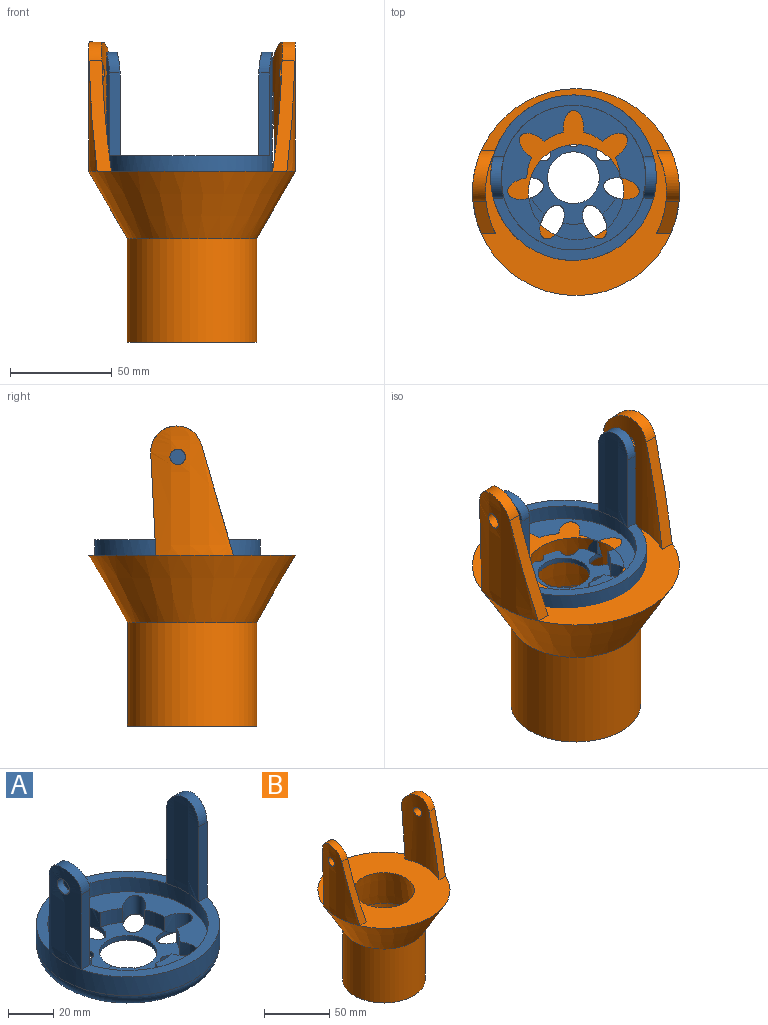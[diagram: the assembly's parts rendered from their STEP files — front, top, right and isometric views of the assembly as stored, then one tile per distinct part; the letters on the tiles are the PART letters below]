
ASSEMBLY  parts=2 mates=1
PART A: 37 faces, bbox 88x88x68.6 mm
  f0: extruded ~50.8x20.32mm, area 952.4mm2, adj f2,f3,f6,f23,f35
  f1: plane 40.64x5.27mm, normal (0,1,0), area 214.2mm2, adj f4,f24,f30,f32
  f2: plane 40.64x5.27mm, normal (0,1,0), area 214.2mm2, adj f0,f3,f24,f31
  f3: cylinder r=10.16mm len=20.32mm, axis (-1,0,0), area 165.2mm2, adj f0,f2,f6,f31
  f4: cylinder r=10.16mm len=20.32mm, axis (-1,0,0), area 165.2mm2, adj f1,f5,f30,f32
  f5: plane 40.64x5.27mm, normal (0,-1,0), area 214.2mm2, adj f4,f7,f30,f32
  f6: plane 40.64x5.27mm, normal (0,-1,0), area 214.2mm2, adj f0,f3,f7,f31
  f7: plane 78.7x30.48mm, normal (0,0,1), area 503.6mm2, adj f5,f6,f23,f25
  f8: cylinder r=22.86mm len=10.14mm, axis (0,0,1), area 80mm2, adj f9,f11,f26,f28
  f9: extruded ~15.27x13.63mm, area 311.7mm2, adj f8,f21,f26,f27,f28
  f10: cylinder r=22.86mm len=8.13mm, axis (0,0,1), area 80mm2, adj f11,f13,f26,f28
  f11: extruded ~17.44x10.67mm, area 311.7mm2, adj f8,f10,f21,f26,f28
  f12: cylinder r=22.86mm len=10.4mm, axis (0,0,1), area 80mm2, adj f13,f15,f26,f28
  f13: extruded ~16.57x11.93mm, area 311.7mm2, adj f10,f12,f21,f26,f28
  f14: cylinder r=22.86mm len=8.13mm, axis (0,0,1), area 80mm2, adj f15,f17,f26,f28
  f15: extruded ~16.57x11.93mm, area 311.7mm2, adj f12,f14,f21,f26,f28
  f16: cylinder r=22.86mm len=10.14mm, axis (0,0,1), area 80mm2, adj f17,f19,f26,f28
  f17: extruded ~17.44x10.67mm, area 311.7mm2, adj f14,f16,f21,f26,f28
  f18: cylinder r=22.86mm len=9.37mm, axis (0,0,1), area 80mm2, adj f19,f26,f28,f29
  f19: extruded ~15.27x13.63mm, area 311.7mm2, adj f16,f18,f21,f26,f28
  f20: cylinder r=12.7mm len=25.4mm, axis (0,0,1), area 202.7mm2, adj f21,f28
  f21: plane 66.04x66.04mm, normal (0,0,-1), area 1925.5mm2, adj f9,f11,f13,f15,f17,f19,f20,f22
  f22: torus R=33.02mm, axis (0,0,1), area 2848.1mm2, adj f21,f23
  f23: cylinder r=40.64mm len=81.28mm, axis (0,0,1), area 2594.3mm2, adj f0,f7,f22,f24,f30
  f24: plane 78.7x30.48mm, normal (0,0,1), area 503.6mm2, adj f1,f2,f23,f25
  f25: cylinder r=35.56mm len=71.12mm, axis (0,0,1), area 1702.5mm2, adj f7,f24,f26,f31,f32
  f26: plane 71.12x71.12mm, normal (0,0,1), area 1731.4mm2, adj f8,f9,f10,f11,f12,f13,f14,f15
  f27: cylinder r=22.86mm len=9.37mm, axis (0,0,1), area 80mm2, adj f9,f26,f28,f29
  f28: plane 45.72x45.17mm, normal (0,0,1), area 741.3mm2, adj f8,f9,f10,f11,f12,f13,f14,f15
  f29: extruded ~17.78x10.16mm, area 311.7mm2, adj f18,f21,f26,f27,f28
  f30: extruded ~50.8x20.32mm, area 952.5mm2, adj f1,f4,f5,f23,f33
  f31: extruded ~50.8x20.32mm, area 1001.3mm2, adj f2,f3,f6,f25
  f32: extruded ~50.8x20.32mm, area 1001.4mm2, adj f1,f4,f5,f25
  f33: cylinder r=3.81mm len=7.62mm, axis (1,0,0), area 89.1mm2, adj f30,f34
  f34: plane 7.62x7.62mm, normal (1,0,0), area 45.6mm2, adj f33
  f35: cylinder r=3.81mm len=7.62mm, axis (-1,0,0), area 89.1mm2, adj f0,f36
  f36: plane 7.62x7.62mm, normal (-1,0,0), area 45.6mm2, adj f35
PART B: 18 faces, bbox 102x102x147.7 mm
  f0: plane 50.54x8.42mm, normal (0,1,-0.05), area 348.2mm2, adj f3,f8,f12,f14
  f1: plane 50.54x8.42mm, normal (0,1,-0.05), area 348.2mm2, adj f2,f8,f13,f15
  f2: cylinder r=12.7mm len=24.9mm, axis (-1,0,0), area 243.6mm2, adj f1,f4,f13,f15
  f3: cylinder r=12.7mm len=24.9mm, axis (-1,0,0), area 243.6mm2, adj f0,f5,f12,f14
  f4: plane 54.66x16.07mm, normal (0,-0.96,0.28), area 374.5mm2, adj f2,f8,f13,f15
  f5: plane 54.66x16.07mm, normal (0,-0.96,0.28), area 374.5mm2, adj f3,f8,f12,f14
  f6: cylinder r=31.75mm len=63.5mm, axis (0,0,1), area 10134.1mm2, adj f7,f11
  f7: cone r=50.8mm half-angle=30deg, axis (0,0,1), area 9880.8mm2, adj f6,f8,f12,f13
  f8: plane 101.6x95.17mm, normal (0,0,1), area 5890.2mm2, adj f0,f1,f4,f5,f7,f9,f14,f15
  f9: cone r=23.39mm half-angle=10deg, axis (0,0,-1), area 5536.8mm2, adj f8,f10
  f10: cylinder r=29.21mm len=58.42mm, axis (0,0,1), area 9323.4mm2, adj f9,f11
  f11: plane 63.5x63.5mm, normal (0,0,-1), area 486.4mm2, adj f6,f10
  f12: extruded ~63.5x40.64mm, area 1880.6mm2, adj f0,f3,f5,f7,f17
  f13: extruded ~63.5x40.64mm, area 1880.3mm2, adj f1,f2,f4,f7,f16
  f14: cylinder r=44.45mm len=63.5mm, axis (0,0,-1), area 1887.3mm2, adj f0,f3,f5,f8,f17
  f15: cylinder r=44.45mm len=63.5mm, axis (0,0,-1), area 1887.4mm2, adj f1,f2,f4,f8,f16
  f16: cylinder r=3.81mm len=7.62mm, axis (1,0,0), area 154mm2, adj f13,f15
  f17: cylinder r=3.81mm len=7.62mm, axis (1,0,0), area 154mm2, adj f12,f14
PLACE A t=(-1.25,7.08,48.26)mm
PLACE B t=(0,0,-25.4)mm fixed
MATE cylindrical B.f16 <-> A.f33  axis (1,0,0) through (46.9,7.08,106.68)mm
